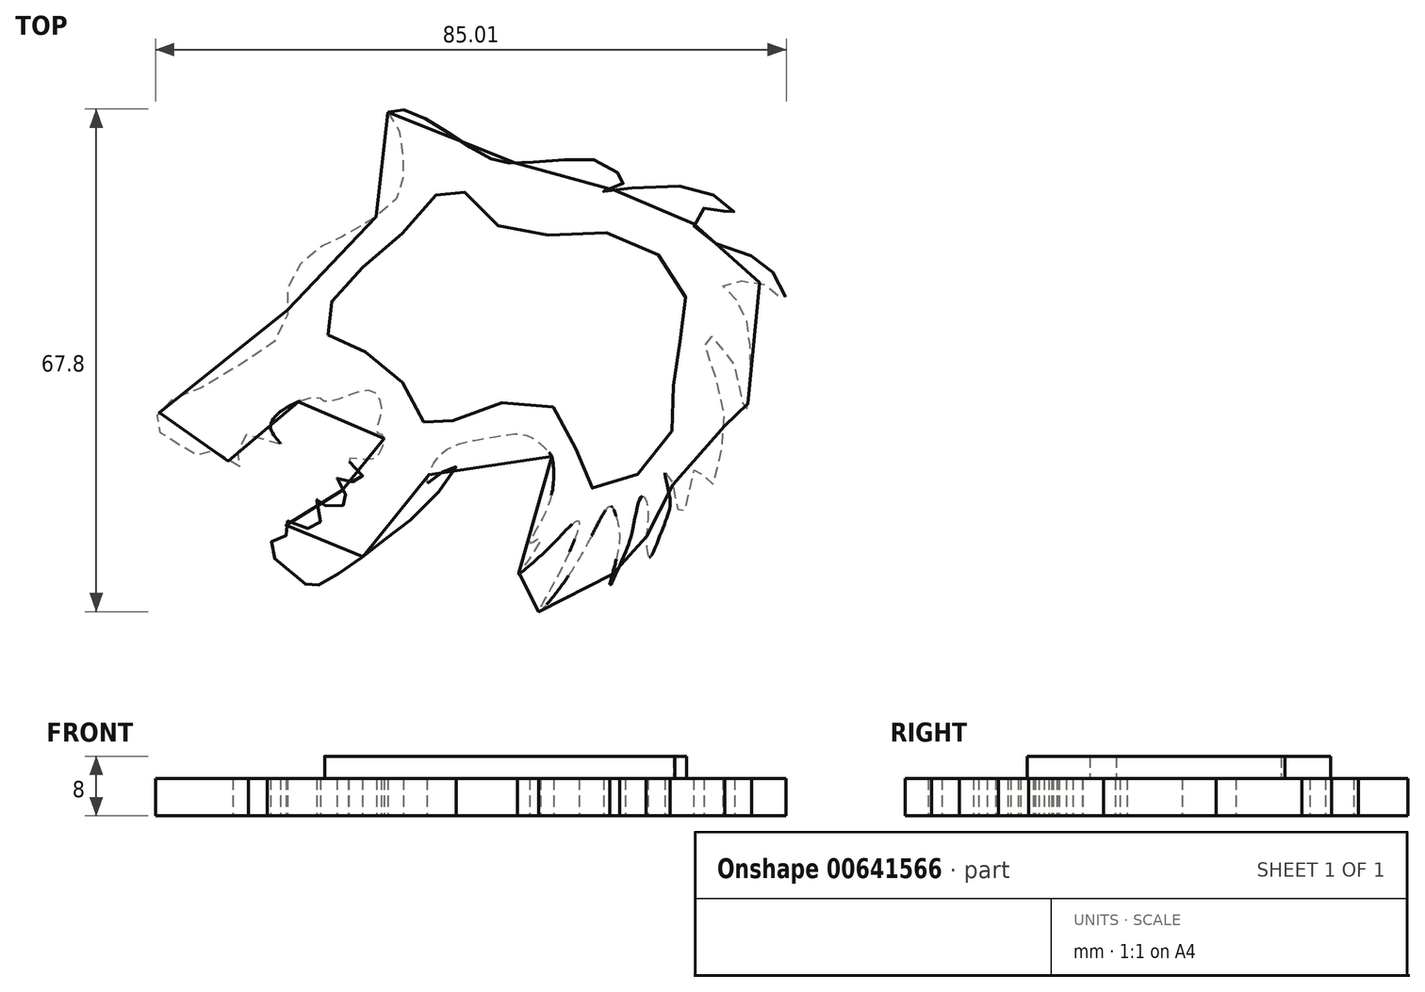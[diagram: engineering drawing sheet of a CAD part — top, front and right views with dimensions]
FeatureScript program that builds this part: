
annotation { "Feature Type Name" : "Feature", "Feature Type Description" : "" }
export const myFeature = defineFeature(function(context is Context, id is Id, definition is map)
    precondition{}
    {
        {
            var Q0;
            Q0=qCreatedBy(makeId("Top.planeOp"),FACE);
            var sketch = newSketch(context, id + "F0", { "sketchPlane" : qUnion([Q0])});
            skFitSpline(sketch, "E0", {"points": [v(-7.3, 36.18) * mm, v(-6.2, 34.6) * mm, v(-5.63, 32.6) * mm, v(-5.3, 30.27) * mm, v(-5.2, 28.02) * mm, v(-5.46, 26.1) * mm, v(-6.38, 24.2) * mm, v(-9.46, 21.7) * mm, v(-13.79, 19.28) * mm, v(-14.62, 19.11) * mm, v(-17.95, 16.7) * mm, v(-19.45, 15.28) * mm, v(-20.86, 12.29) * mm, v(-20.86, 9.7) * mm, v(-21.53, 6.46) * mm, v(-26.2, 2.8) * mm, v(-32.94, -1.2) * mm, v(-36.52, -2.62) * mm, v(-38.1, -4.29) * mm, v(-38.6, -5.03) * mm, v(-38.35, -6.45) * mm, v(-37.27, -7.7) * mm, v(-35.02, -8.78) * mm, v(-33.44, -9.45) * mm, v(-32.44, -10.36) * mm, v(-31.02, -9.45) * mm, v(-30.02, -10.11) * mm, v(-26.11, -11.7) * mm, v(-28.2, -8.45) * mm, v(-26.28, -7.28) * mm, v(-21.78, -8.53) * mm, v(-23.11, -5.95) * mm, v(-16.7, -2.2) * mm, v(-15.95, -2.79) * mm, v(-12.29, -1.87) * mm, v(-9.37, -1.45) * mm, v(-8.2, -4.2) * mm, v(-8.8, -6.95) * mm, v(-7.96, -7.45) * mm, v(-8.54, -9.95) * mm, v(-10.2, -10.7) * mm, v(-12.62, -10.61) * mm, v(-10.96, -12.53) * mm, v(-10.79, -13.2) * mm, v(-12.45, -13.61) * mm, v(-14.12, -13.2) * mm, v(-13.12, -15.28) * mm, v(-12.62, -16.28) * mm, v(-15.12, -17.28) * mm, v(-16.2, -16.2) * mm, v(-16.87, -16.03) * mm, v(-16.45, -19.52) * mm, v(-18.12, -19.94) * mm, v(-20.95, -19.02) * mm, v(-21.03, -20.86) * mm, v(-22.53, -21.6) * mm, v(-23.53, -22.6) * mm, v(-17.37, -28.02) * mm, v(-16.78, -27.68) * mm, v(-13.62, -25.85) * mm, v(-8.7, -22.19) * mm, v(-2.38, -17.03) * mm, v(1.87, -11.45) * mm, v(-0.96, -13.11) * mm, v(-2.05, -13.86) * mm, v(-1.38, -11.7) * mm, v(0.79, -9.2) * mm, v(4.95, -7.95) * mm, v(8.61, -7.37) * mm, v(11.53, -7.45) * mm, v(14.53, -9.86) * mm, v(14.94, -11.03) * mm, v(14.86, -14.86) * mm, v(12.7, -20.1) * mm, v(11.86, -21.94) * mm, v(13.2, -21.27) * mm, v(11.11, -24.94) * mm, v(10.2, -26.19) * mm, v(14.36, -22.6) * mm, v(18.36, -18.94) * mm, v(16.2, -25.19) * mm, v(13.03, -31.18) * mm, v(18.36, -24.27) * mm, v(22.69, -16.94) * mm, v(23.52, -18.6) * mm, v(23.77, -22.69) * mm, v(22.6, -27.6) * mm, v(24.35, -24.02) * mm, v(25.68, -20.02) * mm, v(26.93, -15.61) * mm, v(27.68, -17.03) * mm, v(27.52, -21.27) * mm, v(27.93, -23.85) * mm, v(29.02, -21.77) * mm, v(30.35, -18.36) * mm, v(30.68, -15.86) * mm, v(30.1, -12.45) * mm, v(30.6, -12.7) * mm, v(31.35, -15.28) * mm, v(32.35, -18.52) * mm, v(34.43, -11.2) * mm, v(35.93, -14.44) * mm, v(37.76, -8.95) * mm, v(37.34, -1.04) * mm, v(35.43, 6.04) * mm, v(39.1, 2.7) * mm, v(40.84, -4.45) * mm, v(41.67, 1.54) * mm, v(41.26, 6.46) * mm, v(40.1, 10.45) * mm, v(37.84, 12.62) * mm, v(39.67, 13.37) * mm, v(43.67, 12.87) * mm, v(45.34, 11.45) * mm, v(46.34, 10.79) * mm, v(45, 13.95) * mm, v(41, 17.03) * mm, v(34.1, 20.28) * mm, v(34.93, 23.03) * mm, v(37.18, 23.11) * mm, v(39.42, 22.36) * mm, v(37.93, 24.11) * mm, v(30.18, 26.28) * mm, v(21.77, 25.53) * mm, v(24.6, 26.7) * mm, v(24.52, 27.2) * mm, v(21.35, 29.52) * mm, v(15.86, 29.69) * mm, v(10.2, 29.36) * mm, v(7.78, 29.44) * mm, v(4.87, 30.77) * mm, v(1.12, 33.19) * mm, v(-2.8, 35.6) * mm, v(-5.88, 36.6) * mm, v(-7.3, 36.18) * mm]});
            skSolve(sketch);
        }
        {
            var Q0;
            Q0 = qSketchRegion(id + "F0", true);
            extrude(context, id + "F1", {"entities" : qUnion([Q0]), "depth" : 5 * mm, "offsetDistance" : 25 * mm});
        }
        {
            var Q0;
            Q0=makeQuery(id+"F1.opExtrude","CAP_FACE",FACE,{"disambiguationData":[OSD([sQuery(id+"F0.wireOp",EDGE,"E0")])],"isStart":false});
            var sketch = newSketch(context, id + "F2", { "sketchPlane" : qUnion([Q0])});
            skFitSpline(sketch, "E1", {"points": [v(-15.37, 6.13) * mm, v(-7.1, 2.03) * mm, v(-1.98, -6.01) * mm, v(4.51, -4) * mm, v(16.35, -4.7) * mm, v(20.06, -14.45) * mm, v(30.35, -8.33) * mm, v(31.2, 1.5) * mm, v(32.83, 11.16) * mm, v(23.47, 19.75) * mm, v(8.54, 20.29) * mm, v(1.57, 26.17) * mm, v(-5.08, 20.13) * mm, v(-13.98, 12.01) * mm, v(-15.37, 6.13) * mm]});
            skSolve(sketch);
        }
        {
            var Q0;
            Q0 = qSketchRegion(id + "F2", true);
            extrude(context, id + "F3", {"entities" : qUnion([Q0]), "operationType" : NewBodyOperationType.ADD, "depth" : 3 * mm, "offsetDistance" : 25 * mm});
        }
    });
